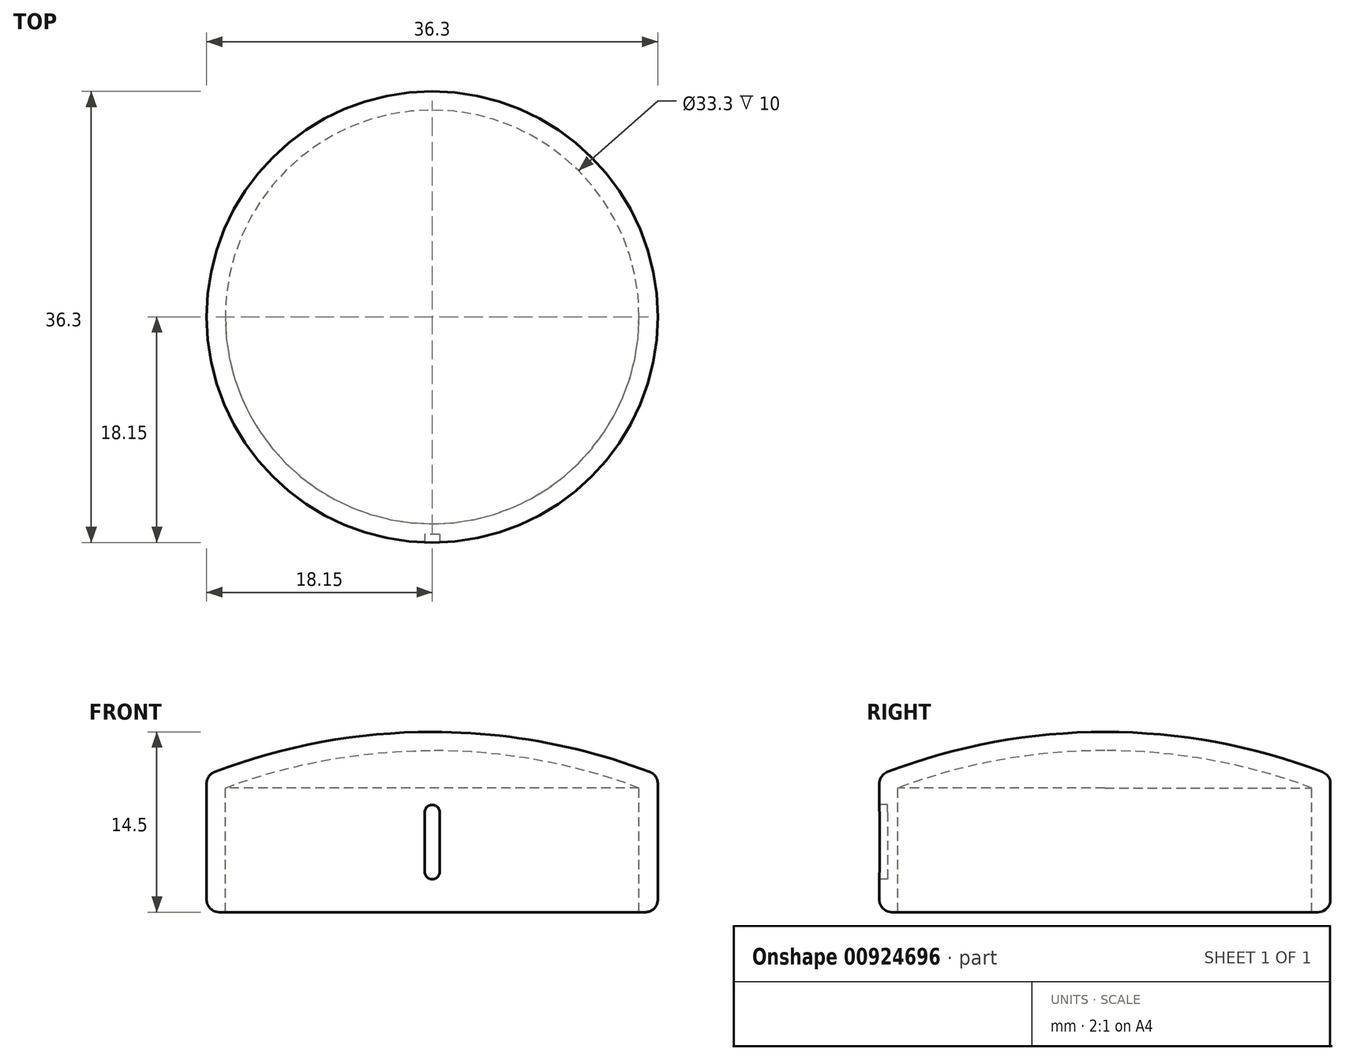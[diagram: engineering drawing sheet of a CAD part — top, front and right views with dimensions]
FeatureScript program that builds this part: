
annotation { "Feature Type Name" : "Feature", "Feature Type Description" : "" }
export const myFeature = defineFeature(function(context is Context, id is Id, definition is map)
    precondition{}
    {
        {
            var Q0;
            Q0=qCreatedBy(makeId("Front.planeOp"),FACE);
            var sketch = newSketch(context, id + "F0", { "sketchPlane" : qUnion([Q0])});
            skLineSegment(sketch, "E0", {"start": v(-16.65, 0) * mm, "end": v(-16.65, 10) * mm});
            skLineSegment(sketch, "E1", {"start": v(0, 10) * mm, "end": v(0, 0) * mm});
            skLineSegment(sketch, "E2", {"start": v(0, 10) * mm, "end": v(16.65, 10) * mm, "construction": true});
            skLineSegment(sketch, "E3", {"start": v(0, 13) * mm, "end": v(0, -19.24) * mm, "construction": true});
            skArc(sketch, "E4", {"start": v(0, 13) * mm, "mid": v(-8.46, 12.24) * mm, "end": v(-16.65, 10) * mm});
            skLineSegment(sketch, "E5.0", {"start": v(-18.15, 1) * mm, "end": v(-18.15, 10.35) * mm});
            skArc(sketch, "E5.1", {"start": v(0, 14.5) * mm, "mid": v(-8.9, 13.69) * mm, "end": v(-17.5, 11.28) * mm});
            skLineSegment(sketch, "E6", {"start": v(-16.65, 0) * mm, "end": v(-17.15, 0) * mm});
            skLineSegment(sketch, "E7", {"start": v(0, 13) * mm, "end": v(0, 14.5) * mm});
            skPoint(sketch, "E8.visualSharp", {"position": v(-18.15, 11.03) * mm});
            skArc(sketch, "E8.filletArc", {"start": v(-17.5, 11.28) * mm, "mid": v(-17.97, 10.91) * mm, "end": v(-18.15, 10.35) * mm});
            skPoint(sketch, "E9.visualSharp", {"position": v(-18.15, 0) * mm});
            skArc(sketch, "E9.filletArc", {"start": v(-18.15, 1) * mm, "mid": v(-17.86, 0.3) * mm, "end": v(-17.15, 0) * mm});
            skSolve(sketch);
        }
        {
            var Q0;
            Q0=makeQuery(id+"F0.imprint","IMPRINT",FACE,{"disambiguationData":[TD([[makeQuery(id+"F0.imprint","IMPRINT",EDGE,{"derivedFrom":sQuery(id+"F0.wireOp",EDGE,"E0")}),1.0]])]});
            var Q1;
            Q1=sQuery(id+"F0.wireOp",EDGE,"E3");
            revolve(context, id + "F1", {"surfaceOperationType" : NewSurfaceOperationType.NEW, "entities" : qUnion([Q0]), "axis" : qUnion([Q1]), "revolveType" : RevolveType.FULL});
        }
        {
            var Q0;
            Q0=qCreatedBy(makeId("Front.planeOp"),FACE);
            cPlane(context, id + "F2", {"entities" : qUnion([Q0]), "cplaneType" : CPlaneType.OFFSET, "offset" : 19 * mm, "width" : 150 * mm, "height" : 150 * mm});
        }
        {
            var Q0;
            Q0=qCreatedBy(id+"F2.planeOp",FACE);
            var sketch = newSketch(context, id + "F3", { "sketchPlane" : qUnion([Q0])});
            skLineSegment(sketch, "E10.bottom", {"start": v(0, 8.64) * mm, "end": v(0, 8.64) * mm});
            skLineSegment(sketch, "E10.top", {"start": v(0, 2.64) * mm, "end": v(0, 2.64) * mm});
            skLineSegment(sketch, "E10.left", {"start": v(-0.6, 8.04) * mm, "end": v(-0.6, 3.24) * mm});
            skLineSegment(sketch, "E10.right", {"start": v(0.6, 8.04) * mm, "end": v(0.6, 3.24) * mm});
            skPoint(sketch, "E11.visualSharp", {"position": v(-0.6, 8.64) * mm});
            skArc(sketch, "E11.filletArc", {"start": v(0, 8.64) * mm, "mid": v(-0.42, 8.46) * mm, "end": v(-0.6, 8.04) * mm});
            skPoint(sketch, "E12.visualSharp", {"position": v(0.6, 8.64) * mm});
            skArc(sketch, "E12.filletArc", {"start": v(0.6, 8.04) * mm, "mid": v(0.42, 8.46) * mm, "end": v(0, 8.64) * mm});
            skPoint(sketch, "E13.visualSharp", {"position": v(-0.6, 2.64) * mm});
            skArc(sketch, "E13.filletArc", {"start": v(-0.6, 3.24) * mm, "mid": v(-0.42, 2.82) * mm, "end": v(0, 2.64) * mm});
            skPoint(sketch, "E14.visualSharp", {"position": v(0.6, 2.64) * mm});
            skArc(sketch, "E14.filletArc", {"start": v(0, 2.64) * mm, "mid": v(0.42, 2.82) * mm, "end": v(0.6, 3.24) * mm});
            skLineSegment(sketch, "E15", {"start": v(0, 11.28) * mm, "end": v(0, 0) * mm, "construction": true});
            skLineSegment(sketch, "E16", {"start": v(0, 5.64) * mm, "end": v(11.65, 5.64) * mm, "construction": true});
            skSolve(sketch);
        }
        {
            var Q0;
            Q0=makeQuery(id+"F3.imprint","IMPRINT",FACE,{"disambiguationData":[TD([[makeQuery(id+"F3.imprint","IMPRINT",EDGE,{"derivedFrom":sQuery(id+"F3.wireOp",EDGE,"E10.left")}),1.0]])]});
            extrude(context, id + "F4", {"entities" : qUnion([Q0]), "operationType" : NewBodyOperationType.REMOVE, "oppositeDirection" : true, "depth" : 1.5 * mm, "offsetDistance" : 25 * mm});
        }
    });
